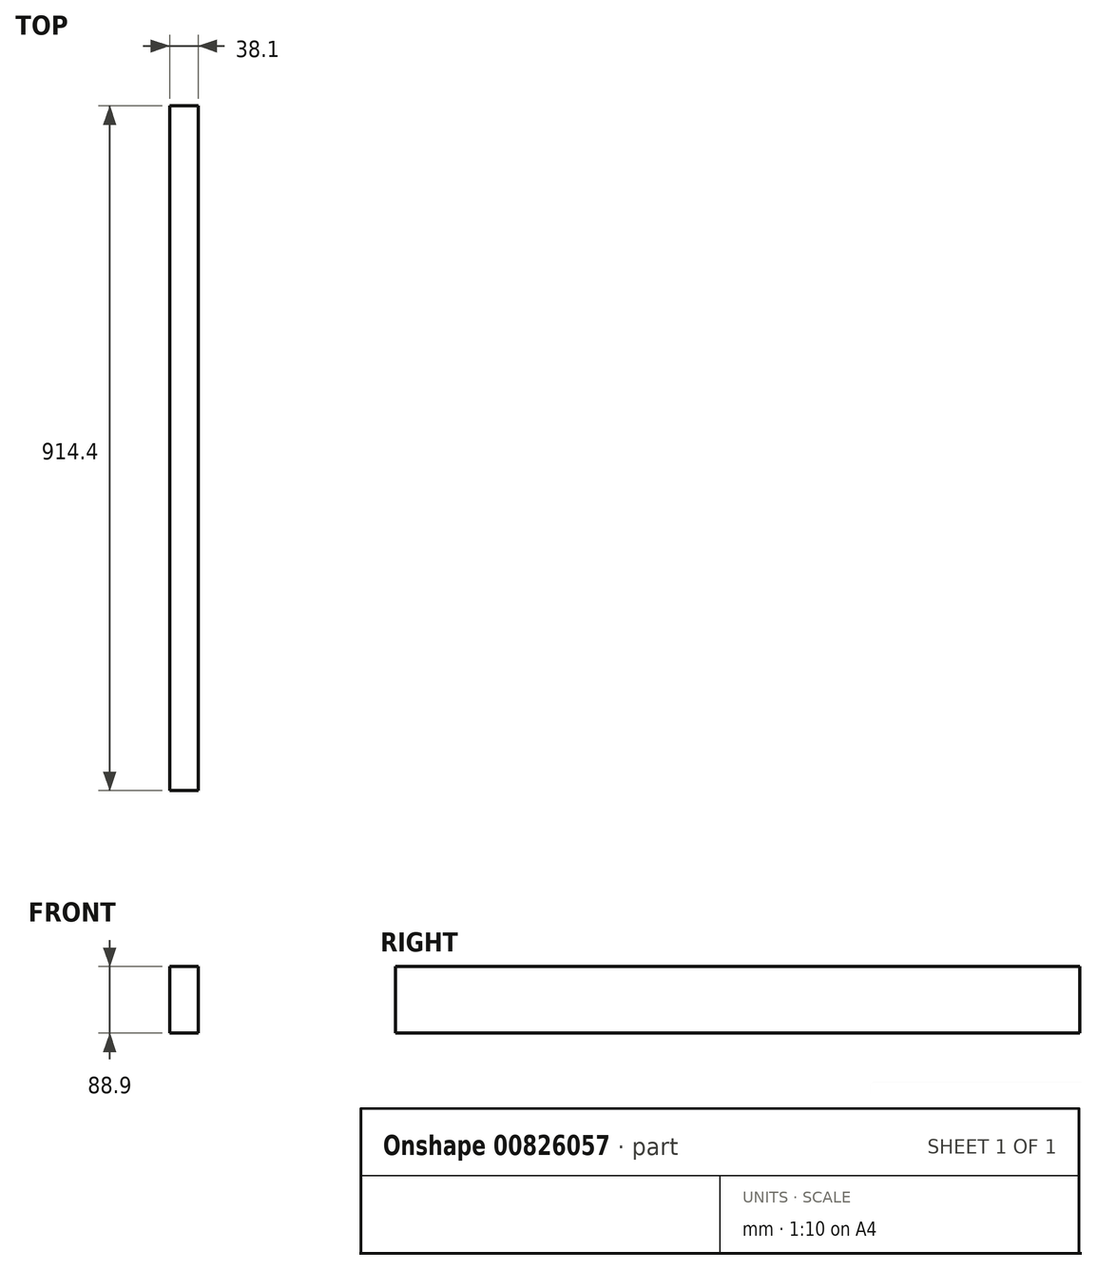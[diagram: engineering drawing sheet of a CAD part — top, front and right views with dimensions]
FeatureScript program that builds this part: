
annotation { "Feature Type Name" : "Feature", "Feature Type Description" : "" }
export const myFeature = defineFeature(function(context is Context, id is Id, definition is map)
    precondition{}
    {
        {
            var Q0;
            Q0=qCreatedBy(makeId("Front.planeOp"),FACE);
            var sketch = newSketch(context, id + "F0", { "sketchPlane" : qUnion([Q0])});
            skLineSegment(sketch, "E0.bottom", {"start": v(-19.05, 44.45) * mm, "end": v(19.05, 44.45) * mm});
            skLineSegment(sketch, "E0.top", {"start": v(-19.05, -44.45) * mm, "end": v(19.05, -44.45) * mm});
            skLineSegment(sketch, "E0.left", {"start": v(-19.05, 44.45) * mm, "end": v(-19.05, -44.45) * mm});
            skLineSegment(sketch, "E0.right", {"start": v(19.05, 44.45) * mm, "end": v(19.05, -44.45) * mm});
            skPoint(sketch, "E0.middle", {"position": v(0, 0) * mm});
            skSolve(sketch);
        }
        {
            var Q0;
            Q0=makeQuery(id+"F0.imprint","IMPRINT",FACE,{"disambiguationData":[TD([[makeQuery(id+"F0.imprint","IMPRINT",EDGE,{"derivedFrom":sQuery(id+"F0.wireOp",EDGE,"E0.bottom")}),-1.0]])]});
            extrude(context, id + "F1", {"entities" : qUnion([Q0]), "endBound" : BoundingType.SYMMETRIC, "depth" : 914.4 * mm, "offsetDistance" : 25.4 * mm});
        }
    });
